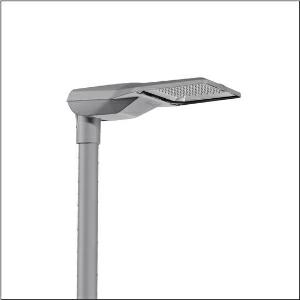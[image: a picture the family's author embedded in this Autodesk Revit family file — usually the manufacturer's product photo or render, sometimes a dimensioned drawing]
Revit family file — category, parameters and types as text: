
# Revit family: streetlight_sl_21_iq_midi___st1_0a_5xe3d31g08mb_3419
name_source: partatom
category: Lighting Fixtures
units: mm (PartAtom-declared; Revit-internal decimal feet)

## family parameters
Cut with Voids When Loaded = No
Host = Face
Light Source = No
Part Type = Normal
Room Calculation Point = No
Round Connector Dimension = Use Diameter
Shared = No

## types (1)
- --- (1 x LED, 19500 lm, 146.7 W, 3000K)
    Apparent Load = 147 VA
    CIE Flux Codes = 37 72 97 100 100
    Color Rendering = 70
    Color Temperature = 3000K
    Default Elevation = 1800 mm
    Description = Streetlight SL 21 iQ midi, mast luminaire, primary light control with lens, of PMMA, primary optical cover: cover, of toughened safety glass, transparent, light distribution: ST1.0a, light emission: direct distribution, primary light characteristic: asymmetric, installation type: post-top, side-entry, LED, High Power LED, rated luminous flux: 19.500lm, luminous efficacy: 133lm/W, light colour: 730, colour temperature: 3000K, control: Street-Remote, Auto-Match, Temp-Guard, Lumen-Switch, Night-Set, Smart-Wire, Light-Fading, Desk-Remote (wireless, voltage-free reading and setting of iQ features in the workshop via application-optimized NFC function/RFID function), optimised constant luminous flux control (CLO 2.0), presetting dimming linear, mains connection: 230..240V, AC, 50/60Hz, start of lifetime: 147W, end of service life: 161W, reduction: 62W, luminaire housing, of diecast aluminium, powder-coated, Siteco® metallic grey (DB 702S), corrosivity category C5 mid according to DIN EN ISO 12944, please order mast flange separately, inclination adjustable: 0°, 5°, 10°, 15°, sealing non-destructively replaceable, multi-level sealing system, length: 644mm, width: 335mm, height: 110mm, mast flange for spigot size: 42mm (side-entry): 5XC10008XM4, 60/48mm (side-entry/post-top): 5XC10108XM2, 76/60mm (side-entry/post-top): 5XC10108XM1, protection rating (complete): IP66, insulation class (complete): insulation class II (safety insulation), certification: CE, ENEC, ENEC+, VDE, impact resistance: IK09, permissible operating ambient temperature for outdoor applications: -40..+50°C, standard-compliant lighting for roads and squares, packaging unit: 1 piece

Light Distribution: ST1.0a
    Height = 111 mm
    Lamp = 1 x LED
    Lamp Light Flux = 19500 lm
    Lamp Power = 146.7 W
    Lamp count = 1
    Length = 644 mm
    Luminous efficacy = 133 lm/W
    Manufacturer = Siteco
    ModVariant = No
    Model = 5XE3D31G08MB
    Number of Poles = 1
    OnlyDefault = Yes
    Power Factor = 1
    Product Name = Streetlight SL 21 iQ midi | ST1.0a
    Product group = mast luminaire | pylon top
    ProductGroupID = 6100
    Protection Class = Protection class II
    Protection Degree = IP 66
    RLX_Detail_Level = 1
    RLX_Emergency_Light_Flux = 0 lm
    RLX_Emergency_Type = 0
    RLX_Emergency_Type_DB = No
    RlxData = <blob elided: 90525 chars, md5=503be4b6>
    Socket = socket
    Standby Power = 0 W
    System Light Flux = 19499 lm
    System Power = 147 W
    Type Comments = factory setting: luminous flux: 100 % | dim-lin: 254 | 753 mA
    Type Image = l_1004298.jpg
    URL = http://relux.com
    VarID = @adj_141819
    Voltage = 0 V
    Weight = 0.00 kg
    Width = 336 mm

## geometry (parser evidence)
native form markers: Blend x4, Sweep x10
no freeform markers — native parametric forms only
